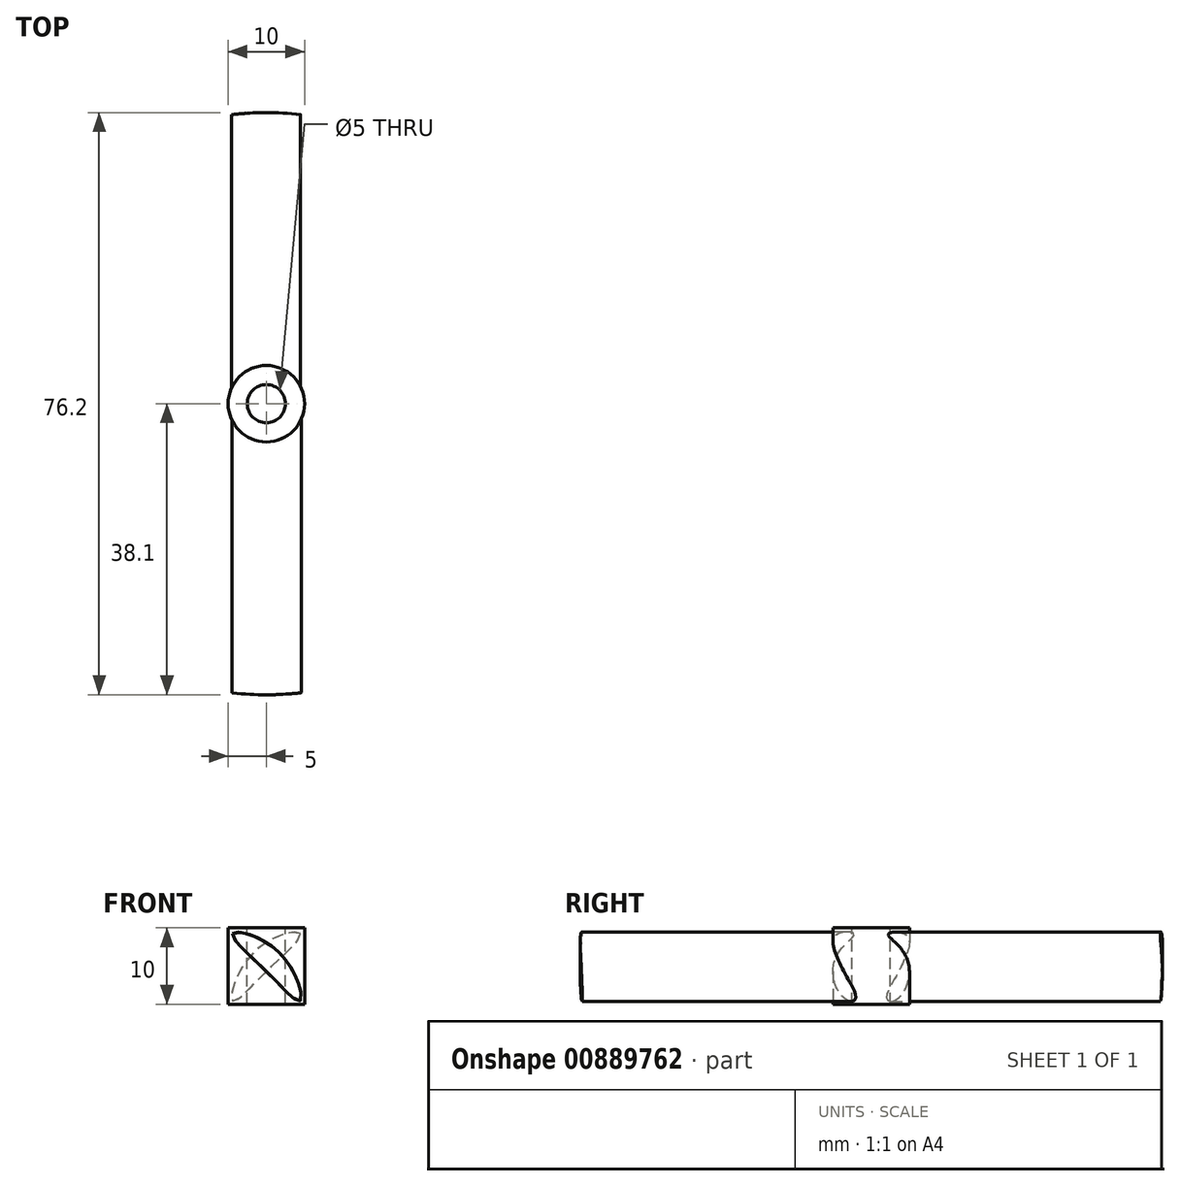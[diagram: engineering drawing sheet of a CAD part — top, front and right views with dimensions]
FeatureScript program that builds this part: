
annotation { "Feature Type Name" : "Feature", "Feature Type Description" : "" }
export const myFeature = defineFeature(function(context is Context, id is Id, definition is map)
    precondition{}
    {
        {
            var Q0;
            Q0=qCreatedBy(makeId("Top.planeOp"),FACE);
            var sketch = newSketch(context, id + "F0", { "sketchPlane" : qUnion([Q0])});
            skCircle(sketch, "E0", {"center": v(0, 0) * mm, "radius": 5 * mm});
            skSolve(sketch);
        }
        {
            var Q0;
            Q0=makeQuery(id+"F0.imprint","IMPRINT",FACE,{"disambiguationData":[TD([[makeQuery(id+"F0.imprint","IMPRINT",EDGE,{"derivedFrom":sQuery(id+"F0.wireOp",EDGE,"E0")}),1.0]])]});
            extrude(context, id + "F1", {"entities" : qUnion([Q0]), "depth" : 10 * mm});
        }
        {
            var Q0;
            Q0=qCreatedBy(makeId("Front.planeOp"),FACE);
            var sketch = newSketch(context, id + "F2", { "sketchPlane" : qUnion([Q0])});
            skFitSpline(sketch, "E1", {"points": [v(-4.43, 9.26) * mm, v(1.62, 6.82) * mm, v(4.45, 0.45) * mm, v(0, 4.28) * mm, v(-4.43, 9.26) * mm]});
            skSolve(sketch);
        }
        {
            var Q0;
            Q0=qSketchRegion(id+"F2",true);
            extrude(context, id + "F3", {"entities" : qUnion([Q0]), "depth" : 100 * mm});
        }
        {
            var Q0;
            Q0=makeQuery(id+"F3.opExtrude","SWEPT_BODY",BODY,{"disambiguationData":[OSD([sQuery(id+"F2.wireOp",EDGE,"E1")])]});
            var Q1;
            Q1=makeQuery(id+"F1.opExtrude","CAP_EDGE",EDGE,{"disambiguationData":[OSD([sQuery(id+"F0.wireOp",EDGE,"E0")])],"isStart":false});
            circularPattern(context, id + "F4", {"operationType" : NewBodyOperationType.ADD, "entities" : qUnion([Q0]), "axis" : qUnion([Q1]), "angle" : 360 * degree, "instanceCount" : 2, "equalSpace" : true});
        }
        {
            var Q0;
            Q0=makeQuery(id+"F1.opExtrude","CAP_FACE",FACE,{"disambiguationData":[OSD([sQuery(id+"F0.wireOp",EDGE,"E0")])],"isStart":false});
            var sketch = newSketch(context, id + "F5", { "sketchPlane" : qUnion([Q0])});
            skCircle(sketch, "E2", {"center": v(0, 0) * mm, "radius": 38.1 * mm});
            skCircle(sketch, "E3", {"center": v(0, 0) * mm, "radius": 106.33 * mm});
            skCircle(sketch, "E4", {"center": v(0, 0) * mm, "radius": 2.5 * mm});
            skSolve(sketch);
        }
        {
            var Q0;
            Q0=makeQuery(id+"F5.imprint","IMPRINT",FACE,{"disambiguationData":[TD([[makeQuery(id+"F5.imprint","IMPRINT",EDGE,{"derivedFrom":sQuery(id+"F5.wireOp",EDGE,"E2")}),-1.0]])]});
            var Q1;
            Q1=makeQuery(id+"F5.imprint","IMPRINT",FACE,{"disambiguationData":[TD([[makeQuery(id+"F5.imprint","IMPRINT",EDGE,{"derivedFrom":sQuery(id+"F5.wireOp",EDGE,"E4")}),1.0]])]});
            extrude(context, id + "F6", {"entities" : qUnion([Q0, Q1]), "operationType" : NewBodyOperationType.REMOVE, "oppositeDirection" : true, "depth" : 25 * mm});
        }
    });
